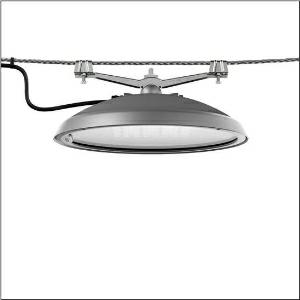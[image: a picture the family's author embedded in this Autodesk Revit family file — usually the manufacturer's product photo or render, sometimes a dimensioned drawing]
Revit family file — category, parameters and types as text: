
# Revit family: dl_50_iq_mini___st1_0s_5xa248w31f08ge_a0c4
name_source: partatom
category: Lighting Fixtures
units: mm (PartAtom-declared; Revit-internal decimal feet)

## family parameters
Cut with Voids When Loaded = No
Host = Face
Light Source = No
Part Type = Normal
Room Calculation Point = No
Round Connector Dimension = Use Diameter
Shared = No

## types (1)
- --- (1 x LED, 5190 lm, 32.7 W, 3000K)
    Apparent Load = 33 VA
    CIE Flux Codes = 37 72 97 100 100
    Color Rendering = 70
    Color Temperature = 3000K
    Default Elevation = 1800 mm
    Description = DL 50 iQ mini, catenary luminaire, primary light control with lens, of PMMA, primary optical cover: cover, of toughened safety glass, transparent, light distribution: ST1.0s, light emission: direct distribution, primary light characteristic: symmetric, installation type: suspended mounting, LED, High Power LED, rated luminous flux: 5.190lm, luminous efficacy: 159lm/W, light colour: 730, colour temperature: 3000K, control gear: iQ Street-Remote, control: optimised constant luminous flux control (CLO 2.0), Desk-Remote (wireless, voltage-free reading and setting of iQ features in the workshop via application-optimized NFC function/RFID function), Light-Fading, Smart-Wire, Night-Set, Lumen-Switch, Temp-Guard, Auto-Match, Street-Remote, mains connection: 230..240V, AC, 50/60Hz, start of lifetime: 33W, end of service life: 34W, reduction: 16W, luminaire housing, of diecast aluminium, powder-coated, SITECO metallic grey (DB 702S), diameter: 500mm, height: 115mm, mounting height: 4..12m, protection rating (complete): IP66, insulation class (complete): insulation class II (safety insulation), certification: CE, ENEC, ENEC+, VDE, impact resistance: IK08, permissible operating ambient temperature for outdoor applications: -25..+40°C, standard-compliant lighting for roads and squares, packaging unit: 1 piece

Light Distribution: ST1.0s
    Height = 124 mm
    Lamp = 1 x LED
    Lamp Light Flux = 5190 lm
    Lamp Power = 32.7 W
    Lamp count = 1
    Length = 500 mm
    Luminous efficacy = 159 lm/W
    Manufacturer = Siteco
    ModVariant = No
    Model = 5XA248W31F08GE
    Number of Poles = 1
    OnlyDefault = Yes
    Power Factor = 1
    Product Name = DL 50 iQ mini | ST1.0s
    Product group = catenary luminaire
    ProductGroupID = 6300
    Protection Class = Protection class II
    Protection Degree = IP 66
    RLX_Detail_Level = 1
    RLX_Emergency_Light_Flux = 0 lm
    RLX_Emergency_Type = 0
    RLX_Emergency_Type_DB = No
    RlxData = <blob elided: 123905 chars, md5=aae51318>
    Socket = socket
    Standby Power = 0 W
    System Light Flux = 5190 lm
    System Power = 33 W
    Type Comments = factory setting: luminous flux: 100 % | dim-lin: 254 | 340 mA
    Type Image = l_1242791.jpg
    URL = http://relux.com
    VarID = @adj_140363
    Voltage = 0 V
    Weight = 0.00 kg
    Width = 0 mm  [stored 0 ft]

note: [stored X ft] marks values corroborated as IEEE doubles in the binary element streams (Revit-internal decimal feet)

## geometry (parser evidence)
native form markers: Blend x4, Sweep x12
no freeform markers — native parametric forms only
